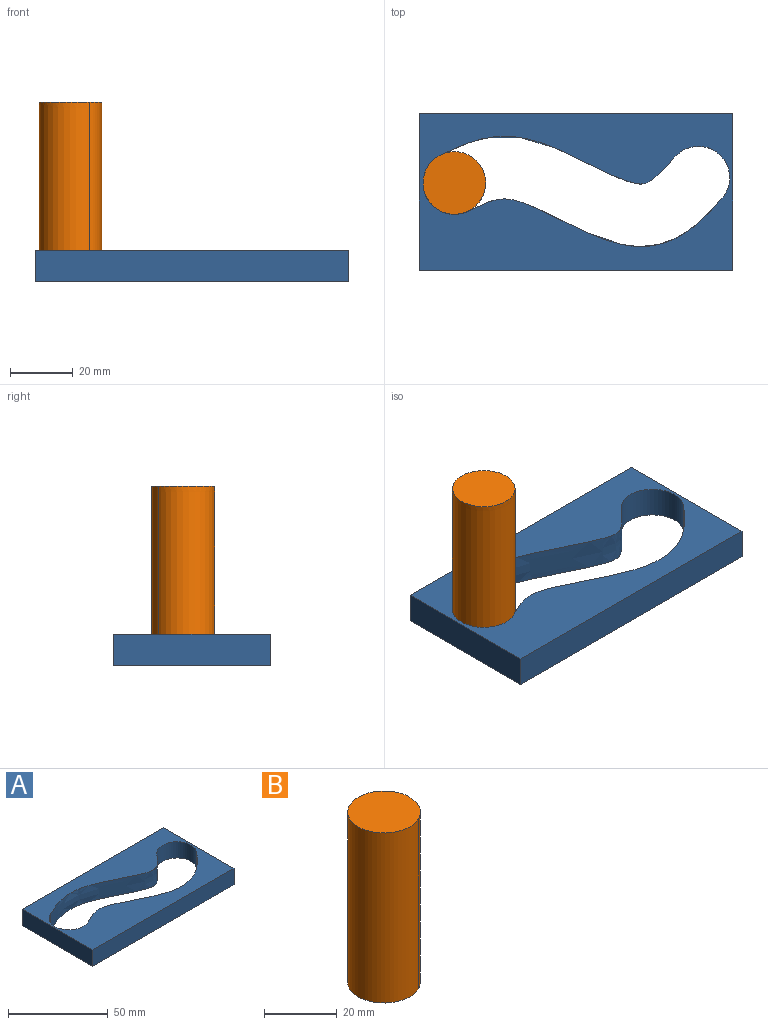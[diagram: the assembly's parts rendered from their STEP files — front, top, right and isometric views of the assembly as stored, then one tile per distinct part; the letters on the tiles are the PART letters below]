
ASSEMBLY  parts=2 mates=1
PART A: 10 faces, bbox 100x50x10 mm
  f0: plane 50x10mm, normal (1,0,0), area 500mm2, adj f1,f3,f4,f5
  f1: plane 100x10mm, normal (0,1,0), area 1000mm2, adj f0,f2,f4,f5
  f2: plane 50x10mm, normal (-1,0,0), area 500mm2, adj f1,f3,f4,f5
  f3: plane 100x10mm, normal (0,-1,0), area 1000mm2, adj f0,f2,f4,f5
  f4: plane 100x50mm, normal (0,0,1), area 2962.2mm2, adj f0,f1,f2,f3,f6,f7,f8,f9
  f5: plane 100x50mm, normal (0,0,-1), area 2962.2mm2, adj f0,f1,f2,f3,f6,f7,f8,f9
  f6: extruded ~74.93x15.18mm, area 823.5mm2, adj f4,f5,f7,f9
  f7: cylinder r=10mm len=18.95mm, axis (0,0,1), area 314.2mm2, adj f4,f5,f6,f8
  f8: extruded ~80.99x15.35mm, area 900.1mm2, adj f4,f5,f7,f9
  f9: cylinder r=10mm len=17.5mm, axis (0,0,1), area 314.2mm2, adj f4,f5,f6,f8
PART B: 4 faces, bbox 20x20x57.2 mm
  f0: cylinder r=10mm len=57.2mm, axis (0,0,-1), area 1797mm2, adj f1,f2,f3
  f1: extruded ~57.2x18.94mm, area 1797.3mm2, adj f0,f2,f3
  f2: plane 20x20mm, normal (0,0,1), area 314.1mm2, adj f0,f1
  f3: plane 20x20mm, normal (0,0,-1), area 314.1mm2, adj f0,f1
PLACE A t=(-22.09,2.28,-6.05)mm fixed
PLACE B rot(axis=(0,0,-1),167.9deg) t=(-99.52,-0.35,-6.05)mm
MATE planar B.f0 <-> A.f5  axis (0,0,-1) through (-60.94,5.08,-6.05)mm
